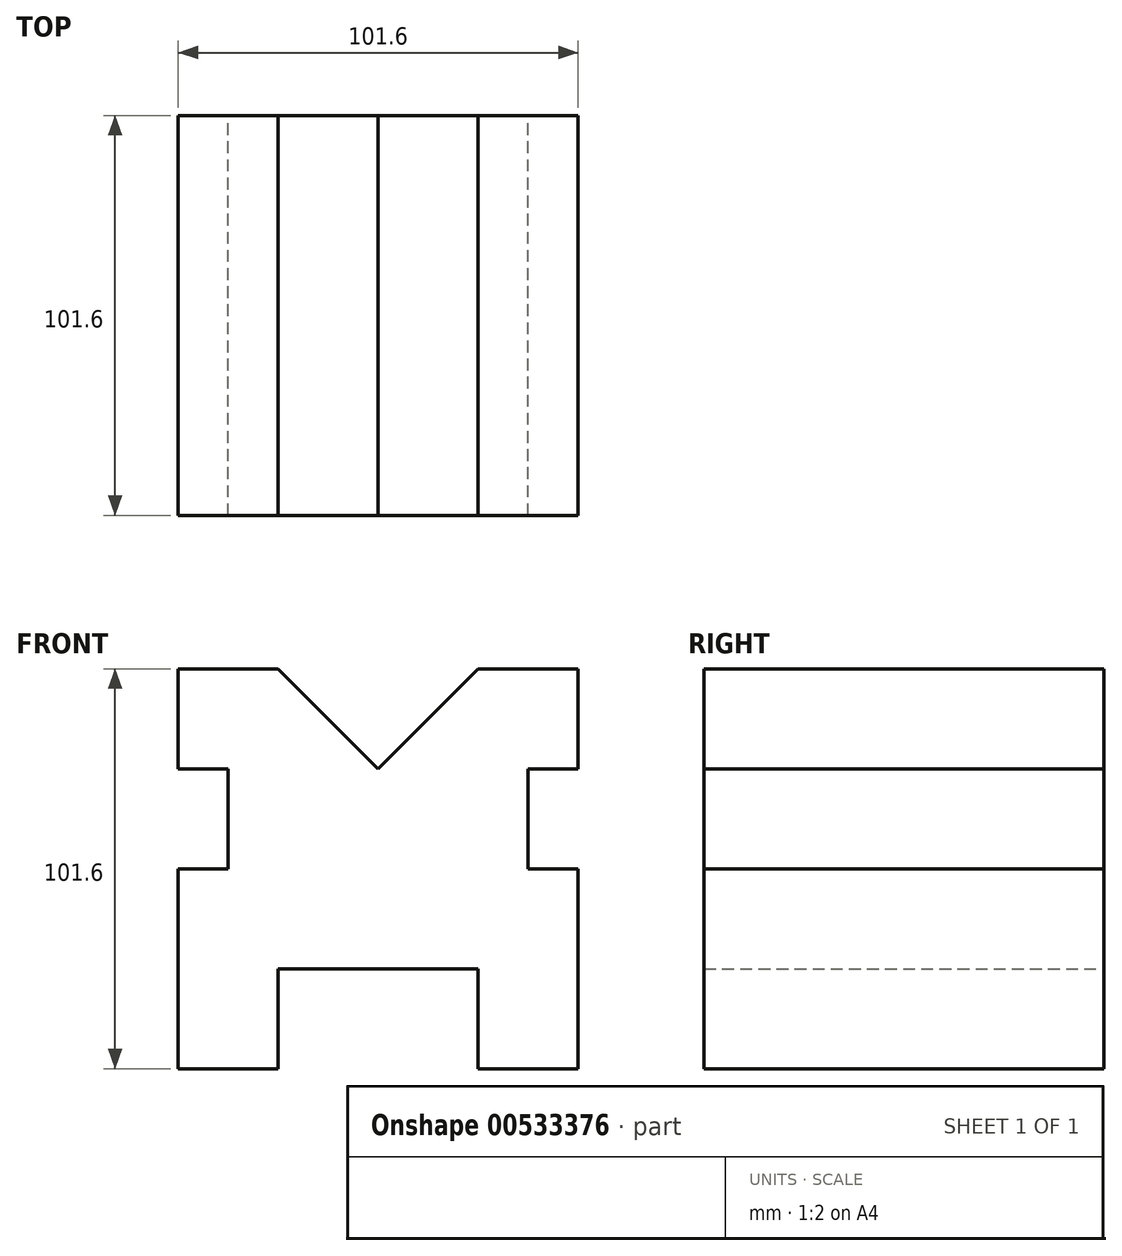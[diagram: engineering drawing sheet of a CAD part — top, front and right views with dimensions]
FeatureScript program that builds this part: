
annotation { "Feature Type Name" : "Feature", "Feature Type Description" : "" }
export const myFeature = defineFeature(function(context is Context, id is Id, definition is map)
    precondition{}
    {
        {
            var Q0;
            Q0=qCreatedBy(makeId("Front.planeOp"),FACE);
            var sketch = newSketch(context, id + "F0", { "sketchPlane" : qUnion([Q0])});
            skLineSegment(sketch, "E0", {"start": v(-39.99, -41.87) * mm, "end": v(-39.99, 8.93) * mm});
            skLineSegment(sketch, "E1", {"start": v(-39.99, 8.93) * mm, "end": v(-27.29, 8.93) * mm});
            skLineSegment(sketch, "E2", {"start": v(-27.29, 8.93) * mm, "end": v(-27.29, 34.33) * mm});
            skLineSegment(sketch, "E3", {"start": v(-27.29, 34.33) * mm, "end": v(-39.99, 34.33) * mm});
            skLineSegment(sketch, "E4", {"start": v(-39.99, 34.33) * mm, "end": v(-39.99, 59.73) * mm});
            skLineSegment(sketch, "E5", {"start": v(-39.99, -41.87) * mm, "end": v(-14.59, -41.87) * mm});
            skLineSegment(sketch, "E6", {"start": v(-14.59, -41.87) * mm, "end": v(-14.59, -16.47) * mm});
            skLineSegment(sketch, "E7", {"start": v(-14.59, -16.47) * mm, "end": v(36.21, -16.47) * mm});
            skLineSegment(sketch, "E8", {"start": v(36.21, -16.47) * mm, "end": v(36.21, -41.87) * mm});
            skLineSegment(sketch, "E9", {"start": v(36.21, -41.87) * mm, "end": v(61.61, -41.87) * mm});
            skLineSegment(sketch, "E10", {"start": v(61.61, -41.87) * mm, "end": v(61.61, 8.93) * mm});
            skLineSegment(sketch, "E11", {"start": v(61.61, 8.93) * mm, "end": v(48.91, 8.93) * mm});
            skLineSegment(sketch, "E12", {"start": v(48.91, 8.93) * mm, "end": v(48.91, 34.33) * mm});
            skLineSegment(sketch, "E13", {"start": v(48.91, 34.33) * mm, "end": v(61.61, 34.33) * mm});
            skLineSegment(sketch, "E14", {"start": v(61.61, 34.33) * mm, "end": v(61.61, 59.73) * mm});
            skLineSegment(sketch, "E15", {"start": v(-39.99, 59.73) * mm, "end": v(-14.59, 59.73) * mm});
            skLineSegment(sketch, "E16", {"start": v(61.61, 59.73) * mm, "end": v(36.21, 59.73) * mm});
            skLineSegment(sketch, "E17", {"start": v(-14.59, 59.73) * mm, "end": v(10.81, 34.33) * mm});
            skLineSegment(sketch, "E18", {"start": v(10.81, 34.33) * mm, "end": v(36.21, 59.73) * mm});
            skSolve(sketch);
        }
        {
            var Q0;
            Q0=makeQuery(id+"F0.imprint","IMPRINT",FACE,{"disambiguationData":[TD([[makeQuery(id+"F0.imprint","IMPRINT",EDGE,{"derivedFrom":sQuery(id+"F0.wireOp",EDGE,"E0")}),-1.0]])]});
            extrude(context, id + "F1", {"entities" : qUnion([Q0]), "depth" : 101.6 * mm, "offsetDistance" : 25.4 * mm});
        }
    });
